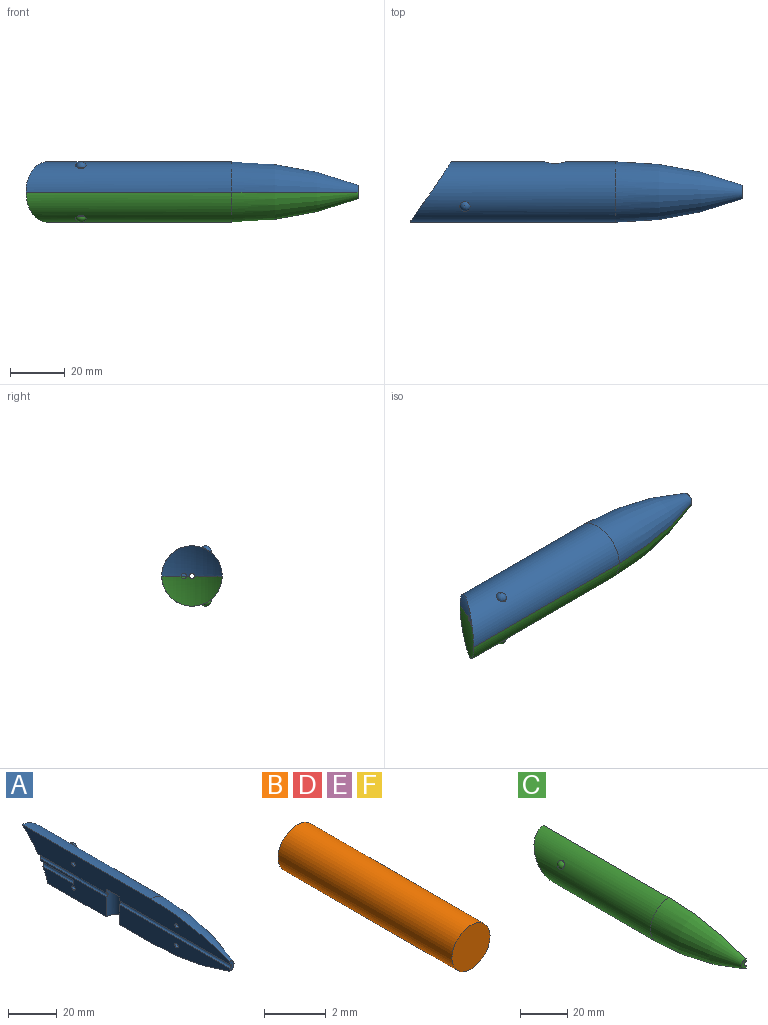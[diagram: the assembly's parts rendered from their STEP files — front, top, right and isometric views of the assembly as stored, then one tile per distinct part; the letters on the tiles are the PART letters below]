
ASSEMBLY  parts=6 mates=5
PART A: 23 faces, bbox 13.3x122.5x22 mm
  f0: cylinder r=11mm len=75mm, axis (0,1,0), area 2292.8mm2, adj f2,f5,f7,f10,f11,f12,f13,f14
  f1: cylinder r=1mm len=64.38mm, axis (0,1,0), area 202.1mm2, adj f3,f5,f13,f14
  f2: revolved ~46x22mm, area 1208mm2, adj f0,f3,f13,f14
  f3: plane 5x2.5mm, normal (0,-1,0), area 8.2mm2, adj f1,f2,f13,f14
  f4: cylinder r=1mm len=39.92mm, axis (0,1,0), area 123.2mm2, adj f5,f7,f12,f13
  f5: cylinder r=3.88mm len=14mm, axis (0,0,1), area 163mm2, adj f0,f1,f4,f6,f12,f13,f14
  f6: plane 7.75x3.88mm, normal (0,0,-1), area 23.6mm2, adj f5,f13
  f7: revolved ~22x16.51mm, area 232.2mm2, adj f0,f4,f9,f12,f13
  f8: plane 2x1mm, normal (0,1,0), area 1.6mm2, adj f9,f12
  f9: cylinder r=1mm len=18.92mm, axis (0,1,0), area 57.7mm2, adj f7,f8,f12
  f10: cylinder r=2mm len=3mm, axis (-1,0,0), area 1.1mm2, adj f0,f11
  f11: sphere r=2mm, area 16.3mm2, adj f0,f10
  f12: plane 38.5x10mm, normal (-1,0,0), area 320.4mm2, adj f0,f4,f5,f7,f8,f9,f21
  f13: plane 121x10mm, normal (-1,0,0), area 1010.2mm2, adj f0,f1,f2,f3,f4,f5,f6,f7
  f14: plane 64.25x10mm, normal (-1,0,0), area 511.9mm2, adj f0,f1,f2,f3,f5,f15
  f15: cylinder r=0.97mm len=4mm, axis (-1,0,0), area 24.5mm2, adj f14,f16
  f16: plane 1.95x1.95mm, normal (-1,0,0), area 3mm2, adj f15
  f17: cylinder r=0.97mm len=4mm, axis (-1,0,0), area 24.5mm2, adj f13,f18
  f18: plane 1.95x1.95mm, normal (-1,0,0), area 3mm2, adj f17
  f19: cylinder r=0.97mm len=4mm, axis (-1,0,0), area 24.5mm2, adj f13,f20
  f20: plane 1.95x1.95mm, normal (-1,0,0), area 3mm2, adj f19
  f21: cylinder r=0.97mm len=4mm, axis (-1,0,0), area 24.5mm2, adj f12,f22
  f22: plane 1.95x1.95mm, normal (-1,0,0), area 3mm2, adj f21
PART B: 3 faces, bbox 1.8x8x1.8 mm
  f0: cylinder r=0.88mm len=8mm, axis (0,1,0), area 44mm2, adj f1,f2
  f1: plane 1.75x1.75mm, normal (0,-1,0), area 2.4mm2, adj f0
  f2: plane 1.75x1.75mm, normal (0,1,0), area 2.4mm2, adj f0
PART C: 23 faces, bbox 13.3x122.5x22 mm
  f0: cylinder r=11mm len=75mm, axis (0,1,0), area 2292.7mm2, adj f2,f5,f7,f10,f11,f12,f13,f14
  f1: cylinder r=1mm len=64.38mm, axis (0,1,0), area 202.1mm2, adj f3,f5,f13,f14
  f2: revolved ~46x22mm, area 1208mm2, adj f0,f3,f13,f14
  f3: plane 5x2.5mm, normal (0,-1,0), area 8.2mm2, adj f1,f2,f13,f14
  f4: cylinder r=1mm len=39.92mm, axis (0,1,0), area 123.2mm2, adj f5,f7,f12,f13
  f5: cylinder r=3.88mm len=14mm, axis (0,0,1), area 163mm2, adj f0,f1,f4,f6,f12,f13,f14
  f6: plane 7.75x3.88mm, normal (0,0,-1), area 23.6mm2, adj f5,f13
  f7: revolved ~22x16.51mm, area 232.1mm2, adj f0,f4,f9,f12,f13
  f8: plane 2x1mm, normal (0,1,0), area 1.6mm2, adj f9,f12
  f9: cylinder r=1mm len=18.92mm, axis (0,1,0), area 57.7mm2, adj f7,f8,f12
  f10: cylinder r=2mm len=3mm, axis (1,0,0), area 1.1mm2, adj f0,f11
  f11: sphere r=2mm, area 16.3mm2, adj f0,f10
  f12: plane 38.5x10mm, normal (1,0,0), area 320.4mm2, adj f0,f4,f5,f7,f8,f9,f21
  f13: plane 121x10mm, normal (1,0,0), area 1010.2mm2, adj f0,f1,f2,f3,f4,f5,f6,f7
  f14: plane 64.25x10mm, normal (1,0,0), area 511.9mm2, adj f0,f1,f2,f3,f5,f15
  f15: cylinder r=0.97mm len=4mm, axis (1,0,0), area 24.5mm2, adj f14,f16
  f16: plane 1.95x1.95mm, normal (1,0,0), area 3mm2, adj f15
  f17: cylinder r=0.97mm len=4mm, axis (1,0,0), area 24.5mm2, adj f13,f18
  f18: plane 1.95x1.95mm, normal (1,0,0), area 3mm2, adj f17
  f19: cylinder r=0.97mm len=4mm, axis (1,0,0), area 24.5mm2, adj f13,f20
  f20: plane 1.95x1.95mm, normal (1,0,0), area 3mm2, adj f19
  f21: cylinder r=0.97mm len=4mm, axis (1,0,0), area 24.5mm2, adj f12,f22
  f22: plane 1.95x1.95mm, normal (1,0,0), area 3mm2, adj f21
PART D: same geometry as B
PART E: same geometry as B
PART F: same geometry as B
PLACE A rot(axis=(0.58,-0.58,0.58),120deg) t=(-88.73,2.51,-46.56)mm
PLACE B rot(axis=(0.58,0.58,0.58),120deg) t=(-58.73,8.51,-42.56)mm
PLACE C rot(axis=(0.58,-0.58,0.58),120deg) t=(-88.73,2.51,-46.56)mm
PLACE D rot(axis=(0.58,0.58,0.58),120deg) t=(1.27,7.51,-42.56)mm
PLACE E rot(axis=(0.58,0.58,0.58),120deg) t=(-58.73,-3.49,-42.56)mm
PLACE F rot(axis=(0.58,0.58,0.58),120deg) t=(1.27,-2.49,-42.56)mm
MATE fastened E.f0 <-> C.f19  axis (0,0,-1) through (-58.73,-3.49,-50.56)mm
MATE fastened A.f13 <-> C.f13  axis (0,0,-1) through (-35.86,-0.49,-46.56)mm
MATE fastened B.f0 <-> C.f21  axis (0,0,-1) through (-58.73,8.51,-50.56)mm
MATE fastened D.f0 <-> C.f15  axis (0,0,-1) through (1.27,7.51,-50.56)mm
MATE fastened F.f0 <-> C.f17  axis (0,0,-1) through (1.27,-2.49,-50.56)mm
